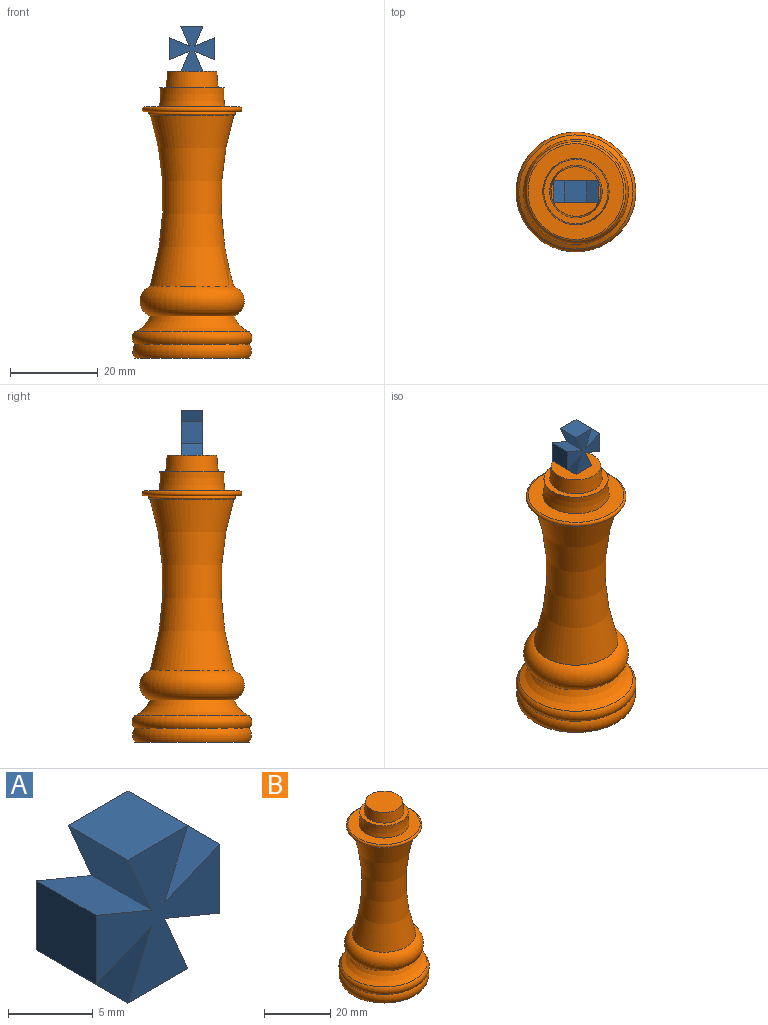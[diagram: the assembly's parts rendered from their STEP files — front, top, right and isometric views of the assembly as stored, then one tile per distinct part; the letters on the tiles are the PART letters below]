
ASSEMBLY  parts=2 mates=1
PART A: 14 faces, bbox 10.3x5x10.4 mm
  f0: plane 5x4.6mm, normal (-0.92,0,0.39), area 25mm2, adj f1,f11,f12,f13
  f1: plane 5x5mm, normal (0,0,-1), area 25mm2, adj f0,f2,f12,f13
  f2: plane 5x4.6mm, normal (0.92,0,0.39), area 25mm2, adj f1,f3,f12,f13
  f3: plane 5x4.62mm, normal (-0.38,0,-0.92), area 25mm2, adj f2,f4,f12,f13
  f4: plane 5x5mm, normal (1,0,0), area 25mm2, adj f3,f5,f12,f13
  f5: plane 5x4.62mm, normal (-0.38,0,0.92), area 25mm2, adj f4,f6,f12,f13
  f6: plane 5x4.6mm, normal (0.92,0,-0.39), area 25mm2, adj f5,f7,f12,f13
  f7: plane 5x5mm, normal (0,0,1), area 25mm2, adj f6,f8,f12,f13
  f8: plane 5x4.6mm, normal (-0.92,0,-0.39), area 25mm2, adj f7,f9,f12,f13
  f9: plane 5x4.62mm, normal (0.38,0,0.92), area 25mm2, adj f8,f10,f12,f13
  f10: plane 5x5mm, normal (-1,0,0), area 25mm2, adj f9,f11,f12,f13
  f11: plane 5x4.62mm, normal (0.38,0,-0.92), area 25mm2, adj f0,f10,f12,f13
  f12: plane 10.36x10.33mm, normal (0,-1,0), area 57.7mm2, adj f0,f1,f2,f3,f4,f5,f6,f7
  f13: plane 10.36x10.33mm, normal (0,1,0), area 57.7mm2, adj f0,f1,f2,f3,f4,f5,f6,f7
PART B: 14 faces, bbox 56.5x56.5x95.4 mm
  f0: torus R=16.1mm, axis (0,0,1), area 357.1mm2, adj f1,f13
  f1: torus R=11.81mm, axis (0,0,1), area 266.5mm2, adj f0,f2
  f2: torus R=10.83mm, axis (0,0,1), area 282.3mm2, adj f1,f3
  f3: plane 26x26mm, normal (0,0,-1), area 530.9mm2, adj f2
  f4: plane 11.27x11.27mm, normal (0,0,1), area 99.8mm2, adj f5
  f5: torus R=43.65mm, axis (0,0,1), area 133.4mm2, adj f4,f6
  f6: plane 14.63x14.63mm, normal (0,0,1), area 56.1mm2, adj f5,f7
  f7: torus R=20.96mm, axis (0,0,1), area 204.5mm2, adj f6,f8
  f8: plane 21.85x21.85mm, normal (0,0,1), area 195.9mm2, adj f7,f9
  f9: torus R=10.81mm, axis (0,0,1), area 110.5mm2, adj f8,f10
  f10: plane 21.85x21.85mm, normal (0,0,-1), area 89.5mm2, adj f9,f11
  f11: torus R=9.53mm, axis (0,0,1), area 72.7mm2, adj f10,f12
  f12: torus R=73.8mm, axis (0,0,1), area 1890.7mm2, adj f11,f13
  f13: torus R=8.37mm, axis (0,0,1), area 616.4mm2, adj f0,f12
PLACE A t=(49.37,9.59,6.4)mm
PLACE B t=(-35.46,7.09,-14.91)mm
MATE fastened A.f1 <-> B.f0  axis (0,0,-1) through (16.93,7.09,59.06)mm
